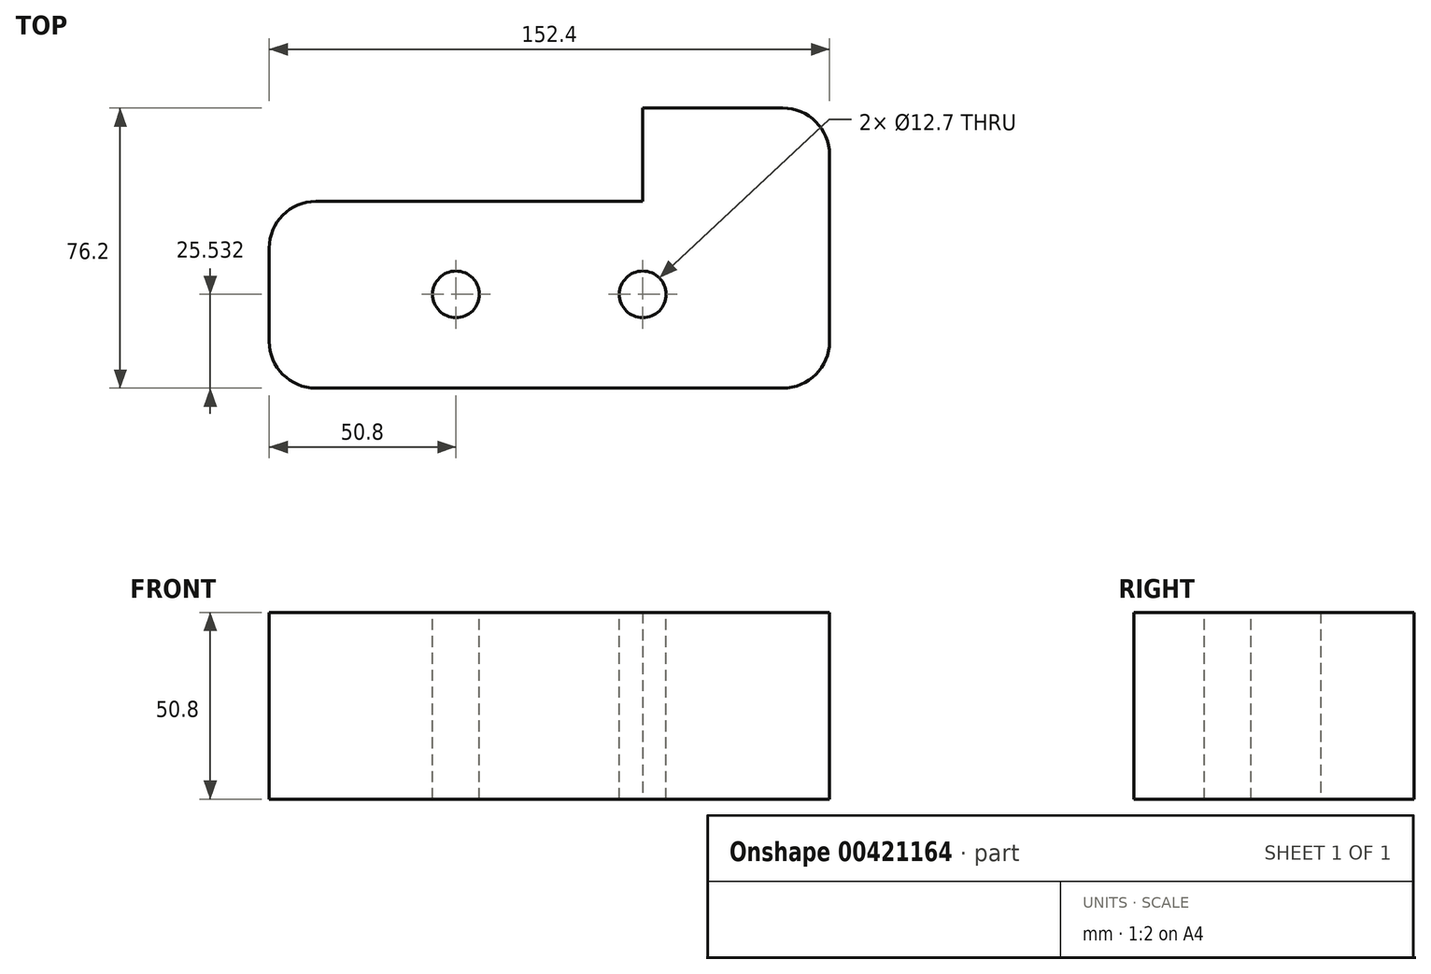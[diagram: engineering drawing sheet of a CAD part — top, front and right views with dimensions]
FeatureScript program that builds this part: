
annotation { "Feature Type Name" : "Feature", "Feature Type Description" : "" }
export const myFeature = defineFeature(function(context is Context, id is Id, definition is map)
    precondition{}
    {
        {
            var Q0;
            Q0=qCreatedBy(makeId("Top.planeOp"),FACE);
            var sketch = newSketch(context, id + "F0", { "sketchPlane" : qUnion([Q0])});
            skLineSegment(sketch, "E0", {"start": v(0, 0) * mm, "end": v(152.4, 0) * mm});
            skLineSegment(sketch, "E1", {"start": v(0, 0) * mm, "end": v(0, 50.8) * mm});
            skLineSegment(sketch, "E2", {"start": v(0, 50.8) * mm, "end": v(101.6, 50.8) * mm});
            skLineSegment(sketch, "E3", {"start": v(101.6, 50.8) * mm, "end": v(101.6, 76.2) * mm});
            skLineSegment(sketch, "E4", {"start": v(101.6, 76.2) * mm, "end": v(152.4, 76.2) * mm});
            skLineSegment(sketch, "E5", {"start": v(152.4, 76.2) * mm, "end": v(152.4, 0) * mm});
            skSolve(sketch);
        }
        {
            var Q0;
            Q0=makeQuery(id+"F0.imprint","IMPRINT",FACE,{"disambiguationData":[TD([[makeQuery(id+"F0.imprint","IMPRINT",EDGE,{"derivedFrom":sQuery(id+"F0.wireOp",EDGE,"E0")}),1.0]])]});
            extrude(context, id + "F1", {"entities" : qUnion([Q0]), "depth" : 50.8 * mm});
        }
        {
            var Q0;
            Q0=makeQuery(id+"F1.opExtrude","SWEPT_EDGE",EDGE,{"disambiguationData":[OSD([sQuery(id+"F0.wireOp",EDGE,"E1"),sQuery(id+"F0.wireOp",EDGE,"E2")])]});
            var Q1;
            Q1=makeQuery(id+"F1.opExtrude","SWEPT_EDGE",EDGE,{"disambiguationData":[OSD([sQuery(id+"F0.wireOp",EDGE,"E4"),sQuery(id+"F0.wireOp",EDGE,"E5")])]});
            var Q2;
            Q2=makeQuery(id+"F1.opExtrude","SWEPT_EDGE",EDGE,{"disambiguationData":[OSD([sQuery(id+"F0.wireOp",EDGE,"E0"),sQuery(id+"F0.wireOp",EDGE,"E5")])]});
            var Q3;
            Q3=makeQuery(id+"F1.opExtrude","SWEPT_EDGE",EDGE,{"disambiguationData":[OSD([sQuery(id+"F0.wireOp",EDGE,"E0"),sQuery(id+"F0.wireOp",EDGE,"E1")])]});
            fillet(context, id + "F2", {"entities" : qUnion([Q0, Q1, Q2, Q3]), "radius" : 12.7 * mm, "tangentPropagation" : true, "allowEdgeOverflow" : false});
        }
        {
            var Q0;
            Q0=makeQuery(id+"F1.opExtrude","CAP_FACE",FACE,{"disambiguationData":[OSD([sQuery(id+"F0.wireOp",EDGE,"E0"),sQuery(id+"F0.wireOp",EDGE,"E1"),sQuery(id+"F0.wireOp",EDGE,"E2"),sQuery(id+"F0.wireOp",EDGE,"E3"),sQuery(id+"F0.wireOp",EDGE,"E4"),sQuery(id+"F0.wireOp",EDGE,"E5")])],"isStart":false});
            var sketch = newSketch(context, id + "F3", { "sketchPlane" : qUnion([Q0])});
            skPoint(sketch, "E6", {"position": v(50.8, 25.53) * mm});
            skPoint(sketch, "E7", {"position": v(101.6, 25.53) * mm});
            skSolve(sketch);
        }
        {
            var Q0;
            Q0=sQuery(id+"F3.wireOp",VERTEX,"E6");
            var Q1;
            Q1=sQuery(id+"F3.wireOp",VERTEX,"E7");
            var Q2;
            Q2=makeQuery(id+"F1.opExtrude","SWEPT_BODY",BODY,{"disambiguationData":[OSD([sQuery(id+"F0.wireOp",EDGE,"E0"),sQuery(id+"F0.wireOp",EDGE,"E1"),sQuery(id+"F0.wireOp",EDGE,"E2"),sQuery(id+"F0.wireOp",EDGE,"E3"),sQuery(id+"F0.wireOp",EDGE,"E4"),sQuery(id+"F0.wireOp",EDGE,"E5")])]});
            hole(context, id + "F4", {"style" : HoleStyle.SIMPLE, "endStyle" : HoleEndStyle.THROUGH, "holeDiameter" : 12.7 * mm, "isTappedThrough" : true, "tappedDepth" : 12.7 * mm, "tapClearance" : 3, "locations" : qUnion([Q0, Q1]), "scope" : qUnion([Q2])});
        }
    });
